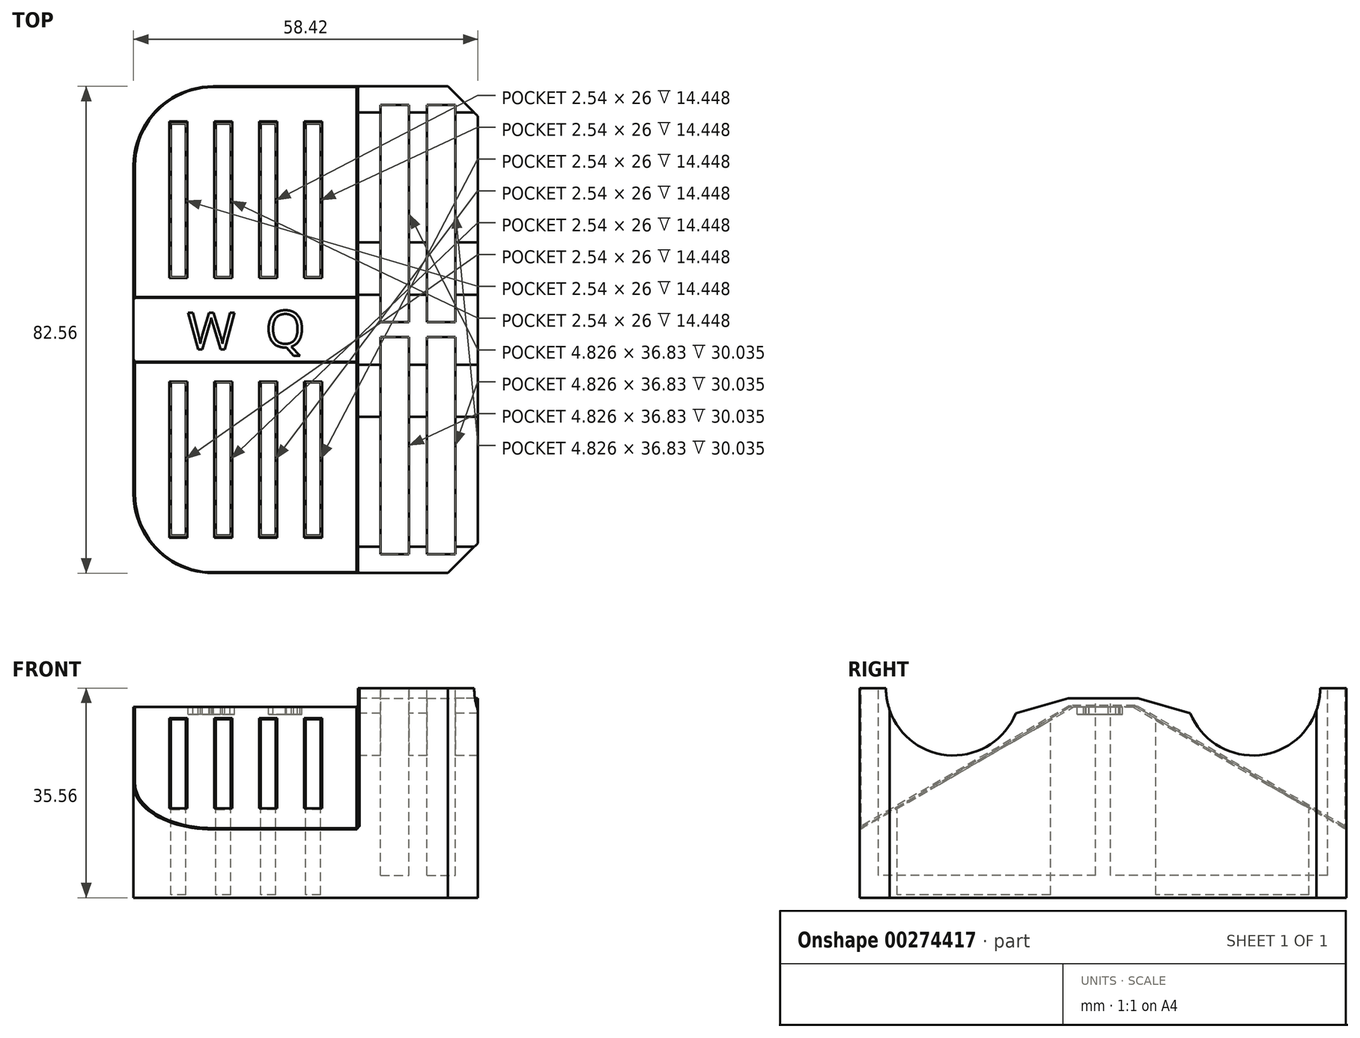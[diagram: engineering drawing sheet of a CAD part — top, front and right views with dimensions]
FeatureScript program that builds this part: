
annotation { "Feature Type Name" : "Feature", "Feature Type Description" : "" }
export const myFeature = defineFeature(function(context is Context, id is Id, definition is map)
    precondition{}
    {
        {
            var Q0;
            Q0=qCreatedBy(makeId("Top.planeOp"),FACE);
            var sketch = newSketch(context, id + "F0", { "sketchPlane" : qUnion([Q0])});
            skLineSegment(sketch, "E0.bottom", {"start": v(-29.2, 41.28) * mm, "end": v(29.21, 41.28) * mm});
            skLineSegment(sketch, "E0.top", {"start": v(-29.21, -41.27) * mm, "end": v(29.2, -41.27) * mm});
            skLineSegment(sketch, "E0.left", {"start": v(-29.2, 41.28) * mm, "end": v(-29.21, -41.27) * mm});
            skLineSegment(sketch, "E0.right", {"start": v(29.21, 41.28) * mm, "end": v(29.2, -41.27) * mm});
            skPoint(sketch, "E0.middle", {"position": v(0, 0) * mm});
            skSolve(sketch);
        }
        {
            var Q0;
            Q0=makeQuery(id+"F0.imprint","IMPRINT",FACE,{"disambiguationData":[TD([[makeQuery(id+"F0.imprint","IMPRINT",EDGE,{"derivedFrom":sQuery(id+"F0.wireOp",EDGE,"E0.bottom")}),-1.0]])]});
            extrude(context, id + "F1", {"entities" : qUnion([Q0]), "depth" : 35.56 * mm});
        }
        {
            var Q0;
            Q0=makeQuery(id+"F1.opExtrude","CAP_FACE",FACE,{"disambiguationData":[OSD([sQuery(id+"F0.wireOp",EDGE,"E0.bottom"),sQuery(id+"F0.wireOp",EDGE,"E0.top"),sQuery(id+"F0.wireOp",EDGE,"E0.left"),sQuery(id+"F0.wireOp",EDGE,"E0.right")])],"isStart":false});
            var sketch = newSketch(context, id + "F2", { "sketchPlane" : qUnion([Q0])});
            skLineSegment(sketch, "E1", {"start": v(-22.86, -8.92) * mm, "end": v(-22.86, -34.92) * mm});
            skLineSegment(sketch, "E2", {"start": v(-22.86, -34.92) * mm, "end": v(-20.32, -34.92) * mm});
            skLineSegment(sketch, "E3", {"start": v(-20.32, -34.92) * mm, "end": v(-20.32, -8.92) * mm});
            skLineSegment(sketch, "E4", {"start": v(-20.32, -8.92) * mm, "end": v(-22.86, -8.92) * mm});
            skLineSegment(sketch, "E5", {"start": v(-15.24, -8.92) * mm, "end": v(-15.24, -34.92) * mm});
            skLineSegment(sketch, "E6", {"start": v(-15.24, -34.92) * mm, "end": v(-12.7, -34.92) * mm});
            skLineSegment(sketch, "E7", {"start": v(-12.7, -34.92) * mm, "end": v(-12.7, -8.92) * mm});
            skLineSegment(sketch, "E8", {"start": v(-12.7, -8.92) * mm, "end": v(-15.24, -8.92) * mm});
            skLineSegment(sketch, "E9", {"start": v(-7.62, -8.92) * mm, "end": v(-7.62, -34.92) * mm});
            skLineSegment(sketch, "E10", {"start": v(-7.62, -34.92) * mm, "end": v(-5.08, -34.92) * mm});
            skLineSegment(sketch, "E11", {"start": v(-5.08, -34.92) * mm, "end": v(-5.08, -8.92) * mm});
            skLineSegment(sketch, "E12", {"start": v(-5.08, -8.92) * mm, "end": v(-7.62, -8.92) * mm});
            skLineSegment(sketch, "E13", {"start": v(0, -8.92) * mm, "end": v(0, -34.92) * mm});
            skLineSegment(sketch, "E14", {"start": v(0, -34.92) * mm, "end": v(2.54, -34.92) * mm});
            skLineSegment(sketch, "E15", {"start": v(2.54, -34.92) * mm, "end": v(2.54, -8.92) * mm});
            skLineSegment(sketch, "E16", {"start": v(2.54, -8.92) * mm, "end": v(0, -8.92) * mm});
            skLineSegment(sketch, "E17", {"start": v(-22.86, 34.93) * mm, "end": v(-22.86, 8.93) * mm});
            skLineSegment(sketch, "E18", {"start": v(-22.86, 8.93) * mm, "end": v(-20.32, 8.93) * mm});
            skLineSegment(sketch, "E19", {"start": v(-20.32, 8.93) * mm, "end": v(-20.32, 34.93) * mm});
            skLineSegment(sketch, "E20", {"start": v(-20.32, 34.93) * mm, "end": v(-22.86, 34.93) * mm});
            skLineSegment(sketch, "E21", {"start": v(-15.24, 34.93) * mm, "end": v(-15.24, 8.93) * mm});
            skLineSegment(sketch, "E22", {"start": v(-15.24, 8.93) * mm, "end": v(-12.7, 8.93) * mm});
            skLineSegment(sketch, "E23", {"start": v(-12.7, 8.93) * mm, "end": v(-12.7, 34.93) * mm});
            skLineSegment(sketch, "E24", {"start": v(-12.7, 34.93) * mm, "end": v(-15.24, 34.93) * mm});
            skLineSegment(sketch, "E25", {"start": v(-7.62, 34.93) * mm, "end": v(-7.62, 8.93) * mm});
            skLineSegment(sketch, "E26", {"start": v(-7.62, 8.93) * mm, "end": v(-5.08, 8.93) * mm});
            skLineSegment(sketch, "E27", {"start": v(-5.08, 8.93) * mm, "end": v(-5.08, 34.93) * mm});
            skLineSegment(sketch, "E28", {"start": v(-5.08, 34.93) * mm, "end": v(-7.62, 34.93) * mm});
            skLineSegment(sketch, "E29", {"start": v(0, 34.93) * mm, "end": v(0, 8.93) * mm});
            skLineSegment(sketch, "E30", {"start": v(0, 8.93) * mm, "end": v(2.54, 8.93) * mm});
            skLineSegment(sketch, "E31", {"start": v(2.54, 8.93) * mm, "end": v(2.54, 34.93) * mm});
            skLineSegment(sketch, "E32", {"start": v(2.54, 34.93) * mm, "end": v(0, 34.93) * mm});
            skSolve(sketch);
        }
        {
            var Q0;
            Q0=makeQuery(id+"F2.imprint","IMPRINT",FACE,{"disambiguationData":[TD([[makeQuery(id+"F2.imprint","IMPRINT",EDGE,{"derivedFrom":sQuery(id+"F2.wireOp",EDGE,"E17")}),1.0]])]});
            var Q1;
            Q1=makeQuery(id+"F2.imprint","IMPRINT",FACE,{"disambiguationData":[TD([[makeQuery(id+"F2.imprint","IMPRINT",EDGE,{"derivedFrom":sQuery(id+"F2.wireOp",EDGE,"E21")}),1.0]])]});
            var Q2;
            Q2=makeQuery(id+"F2.imprint","IMPRINT",FACE,{"disambiguationData":[TD([[makeQuery(id+"F2.imprint","IMPRINT",EDGE,{"derivedFrom":sQuery(id+"F2.wireOp",EDGE,"E25")}),1.0]])]});
            var Q3;
            Q3=makeQuery(id+"F2.imprint","IMPRINT",FACE,{"disambiguationData":[TD([[makeQuery(id+"F2.imprint","IMPRINT",EDGE,{"derivedFrom":sQuery(id+"F2.wireOp",EDGE,"E29")}),1.0]])]});
            var Q4;
            Q4=makeQuery(id+"F2.imprint","IMPRINT",FACE,{"disambiguationData":[TD([[makeQuery(id+"F2.imprint","IMPRINT",EDGE,{"derivedFrom":sQuery(id+"F2.wireOp",EDGE,"E13")}),1.0]])]});
            var Q5;
            Q5=makeQuery(id+"F2.imprint","IMPRINT",FACE,{"disambiguationData":[TD([[makeQuery(id+"F2.imprint","IMPRINT",EDGE,{"derivedFrom":sQuery(id+"F2.wireOp",EDGE,"E9")}),1.0]])]});
            var Q6;
            Q6=makeQuery(id+"F2.imprint","IMPRINT",FACE,{"disambiguationData":[TD([[makeQuery(id+"F2.imprint","IMPRINT",EDGE,{"derivedFrom":sQuery(id+"F2.wireOp",EDGE,"E5")}),1.0]])]});
            var Q7;
            Q7=makeQuery(id+"F2.imprint","IMPRINT",FACE,{"disambiguationData":[TD([[makeQuery(id+"F2.imprint","IMPRINT",EDGE,{"derivedFrom":sQuery(id+"F2.wireOp",EDGE,"E1")}),1.0]])]});
            extrude(context, id + "F3", {"entities" : qUnion([Q0, Q1, Q2, Q3, Q4, Q5, Q6, Q7]), "operationType" : NewBodyOperationType.REMOVE, "oppositeDirection" : true, "depth" : 35.05 * mm});
        }
        {
            var Q0;
            Q0=makeQuery(id+"F1.opExtrude","SWEPT_FACE",FACE,{"disambiguationData":[OSD([sQuery(id+"F0.wireOp",EDGE,"E0.left")])]});
            var sketch = newSketch(context, id + "F4", { "sketchPlane" : qUnion([Q0])});
            skLineSegment(sketch, "E33", {"start": v(0, 35.56) * mm, "end": v(-41.28, 11.73) * mm});
            skLineSegment(sketch, "E34", {"start": v(0, 35.56) * mm, "end": v(41.27, 11.73) * mm});
            skLineSegment(sketch, "E35", {"start": v(-5.53, 32.37) * mm, "end": v(5.53, 32.37) * mm});
            skSolve(sketch);
        }
        {
            var Q0;
            {var subQ0=sQuery(id+"F4.wireOp",EDGE,"E33");Q0=makeQuery(id+"F4.imprint","IMPRINT",FACE,{"disambiguationData":[TD([[makeQuery(id+"F4.imprint","IMPRINT",EDGE,{"derivedFrom":subQ0}),-1.0]])]});}
            var Q1;
            {var subQ0=sQuery(id+"F4.wireOp",EDGE,"E34");Q1=makeQuery(id+"F4.imprint","IMPRINT",FACE,{"disambiguationData":[TD([[makeQuery(id+"F4.imprint","IMPRINT",EDGE,{"derivedFrom":subQ0}),1.0]])]});}
            var Q2;
            {var subQ3=sQuery(id+"F4.wireOp",EDGE,"E35");Q2=makeQuery(id+"F4.imprint","IMPRINT",FACE,{"disambiguationData":[TD([[makeQuery(id+"F4.imprint","IMPRINT",EDGE,{"derivedFrom":subQ3}),1.0]])]});}
            extrude(context, id + "F5", {"entities" : qUnion([Q0, Q1, Q2]), "operationType" : NewBodyOperationType.REMOVE, "oppositeDirection" : true, "depth" : 38.1 * mm});
        }
        {
            var Q0;
            Q0=makeQuery(id+"F1.opExtrude","CAP_FACE",FACE,{"disambiguationData":[OSD([sQuery(id+"F0.wireOp",EDGE,"E0.bottom"),sQuery(id+"F0.wireOp",EDGE,"E0.top"),sQuery(id+"F0.wireOp",EDGE,"E0.left"),sQuery(id+"F0.wireOp",EDGE,"E0.right")])],"isStart":false});
            var sketch = newSketch(context, id + "F6", { "sketchPlane" : qUnion([Q0])});
            skLineSegment(sketch, "E36.bottom", {"start": v(12.7, -1.27) * mm, "end": v(17.53, -1.27) * mm});
            skLineSegment(sketch, "E36.top", {"start": v(12.7, -38.1) * mm, "end": v(17.53, -38.1) * mm});
            skLineSegment(sketch, "E36.left", {"start": v(12.7, -1.27) * mm, "end": v(12.7, -38.1) * mm});
            skLineSegment(sketch, "E36.right", {"start": v(17.53, -1.27) * mm, "end": v(17.53, -38.1) * mm});
            skLineSegment(sketch, "E37.bottom", {"start": v(12.7, 38.1) * mm, "end": v(17.53, 38.1) * mm});
            skLineSegment(sketch, "E37.top", {"start": v(12.7, 1.27) * mm, "end": v(17.53, 1.27) * mm});
            skLineSegment(sketch, "E37.left", {"start": v(12.7, 38.1) * mm, "end": v(12.7, 1.27) * mm});
            skLineSegment(sketch, "E37.right", {"start": v(17.53, 38.1) * mm, "end": v(17.53, 1.27) * mm});
            skLineSegment(sketch, "E38.bottom", {"start": v(20.57, 38.1) * mm, "end": v(25.4, 38.1) * mm});
            skLineSegment(sketch, "E38.top", {"start": v(20.57, 1.27) * mm, "end": v(25.4, 1.27) * mm});
            skLineSegment(sketch, "E38.left", {"start": v(20.57, 38.1) * mm, "end": v(20.57, 1.27) * mm});
            skLineSegment(sketch, "E38.right", {"start": v(25.4, 38.1) * mm, "end": v(25.4, 1.27) * mm});
            skLineSegment(sketch, "E39.bottom", {"start": v(20.57, -1.27) * mm, "end": v(25.4, -1.27) * mm});
            skLineSegment(sketch, "E39.top", {"start": v(20.57, -38.1) * mm, "end": v(25.4, -38.1) * mm});
            skLineSegment(sketch, "E39.left", {"start": v(20.57, -1.27) * mm, "end": v(20.57, -38.1) * mm});
            skLineSegment(sketch, "E39.right", {"start": v(25.4, -1.27) * mm, "end": v(25.4, -38.1) * mm});
            skSolve(sketch);
        }
        {
            var Q0;
            Q0=makeQuery(id+"F6.imprint","IMPRINT",FACE,{"disambiguationData":[TD([[makeQuery(id+"F6.imprint","IMPRINT",EDGE,{"derivedFrom":sQuery(id+"F6.wireOp",EDGE,"E37.bottom")}),-1.0]])]});
            var Q1;
            Q1=makeQuery(id+"F6.imprint","IMPRINT",FACE,{"disambiguationData":[TD([[makeQuery(id+"F6.imprint","IMPRINT",EDGE,{"derivedFrom":sQuery(id+"F6.wireOp",EDGE,"E38.bottom")}),-1.0]])]});
            var Q2;
            Q2=makeQuery(id+"F6.imprint","IMPRINT",FACE,{"disambiguationData":[TD([[makeQuery(id+"F6.imprint","IMPRINT",EDGE,{"derivedFrom":sQuery(id+"F6.wireOp",EDGE,"E36.bottom")}),-1.0]])]});
            var Q3;
            Q3=makeQuery(id+"F6.imprint","IMPRINT",FACE,{"disambiguationData":[TD([[makeQuery(id+"F6.imprint","IMPRINT",EDGE,{"derivedFrom":sQuery(id+"F6.wireOp",EDGE,"E39.bottom")}),-1.0]])]});
            extrude(context, id + "F7", {"entities" : qUnion([Q0, Q1, Q2, Q3]), "operationType" : NewBodyOperationType.REMOVE, "oppositeDirection" : true, "depth" : 31.75 * mm});
        }
        {
            var Q0;
            Q0=makeQuery(id+"F5.boolean.opBoolean","COPY",FACE,{"derivedFrom":makeQuery(id+"F5.opExtrude","SWEPT_FACE",FACE,{"disambiguationData":[OSD([sQuery(id+"F4.wireOp",EDGE,"E35")])]})});
            var sketch = newSketch(context, id + "F8", { "sketchPlane" : qUnion([Q0])});
            skText(sketch, "E40", { "text": "W", "fontName": "OpenSans-Regular.ttf"});
            skText(sketch, "E41", { "text": "Q\n", "fontName": "OpenSans-Regular.ttf"});
            const initialGuessF8  = {"E40": [-0.02004, -0.00333, 1, 0, 0.0063], "E41": [-0.00682, -0.00293, 1, 0, 0.0062]};
            skSetInitialGuess(sketch, initialGuessF8);
            skSolve(sketch);
        }
        {
            var Q0;
            Q0=qSketchRegion(id+"F8",true);
            extrude(context, id + "F9", {"entities" : qUnion([Q0]), "operationType" : NewBodyOperationType.REMOVE, "oppositeDirection" : true, "depth" : 1.27 * mm});
        }
        {
            var Q0;
            Q0=makeQuery(id+"F5.boolean.opBoolean","COPY",FACE,{"derivedFrom":makeQuery(id+"F5.opExtrude","CAP_FACE",FACE,{"disambiguationData":[OSD([sQuery(id+"F0.wireOp",EDGE,"E0.bottom"),sQuery(id+"F0.wireOp",EDGE,"E0.top"),sQuery(id+"F0.wireOp",EDGE,"E0.left"),sQuery(id+"F4.wireOp",EDGE,"E33"),sQuery(id+"F4.wireOp",EDGE,"E34"),sQuery(id+"F4.wireOp",EDGE,"E35")])],"isStart":false})});
            var sketch = newSketch(context, id + "F10", { "sketchPlane" : qUnion([Q0])});
            skLineSegment(sketch, "E42", {"start": v(-41.28, 23.64) * mm, "end": v(0, 35.56) * mm});
            skLineSegment(sketch, "E43", {"start": v(0, 35.56) * mm, "end": v(41.27, 23.64) * mm});
            skLineSegment(sketch, "E44", {"start": v(-1.27, 35.2) * mm, "end": v(1.27, 35.2) * mm});
            skArc(sketch, "E45", {"start": v(-35.56, 40.8) * mm, "mid": v(-28.1, 24.45) * mm, "end": v(-13.97, 35.56) * mm});
            skArc(sketch, "E46", {"start": v(13.97, 35.56) * mm, "mid": v(25.4, 24.13) * mm, "end": v(36.83, 35.56) * mm});
            skLineSegment(sketch, "E47", {"start": v(-14.1, 33.85) * mm, "end": v(14.1, 33.85) * mm});
            skSolve(sketch);
        }
        {
            var Q0;
            {var subQ0=sQuery(id+"F10.wireOp",EDGE,"E45");var subQ1=sQuery(id+"F10.wireOp",EDGE,"E42");var subQ2=makeQuery(id+"F10.imprint","INTERSECT",VERTEX,{"disambiguationData":[OD(0.0)],"derivedFrom":[subQ1,subQ0]});Q0=makeQuery(id+"F10.imprint","IMPRINT",FACE,{"disambiguationData":[TD([[makeQuery(id+"F10.imprint","IMPRINT",EDGE,{"disambiguationData":[TD([[subQ2,-1.0]])],"derivedFrom":subQ1}),-1.0]])]});}
            var Q1;
            {var subQ0=sQuery(id+"F10.wireOp",EDGE,"E46");var subQ1=sQuery(id+"F10.wireOp",EDGE,"E43");var subQ2=makeQuery(id+"F10.imprint","INTERSECT",VERTEX,{"disambiguationData":[OD(0.0)],"derivedFrom":[subQ1,subQ0]});Q1=makeQuery(id+"F10.imprint","IMPRINT",FACE,{"disambiguationData":[TD([[makeQuery(id+"F10.imprint","IMPRINT",EDGE,{"disambiguationData":[TD([[subQ2,-1.0]])],"derivedFrom":subQ1}),1.0]])]});}
            var Q2;
            {var subQ0=sQuery(id+"F10.wireOp",EDGE,"E46");var subQ1=sQuery(id+"F10.wireOp",EDGE,"E43");var subQ2=makeQuery(id+"F10.imprint","INTERSECT",VERTEX,{"disambiguationData":[OD(0.0)],"derivedFrom":[subQ1,subQ0]});Q2=makeQuery(id+"F10.imprint","IMPRINT",FACE,{"disambiguationData":[TD([[makeQuery(id+"F10.imprint","IMPRINT",EDGE,{"disambiguationData":[TD([[subQ2,-1.0]])],"derivedFrom":subQ1}),-1.0]])]});}
            var Q3;
            {var subQ0=sQuery(id+"F10.wireOp",EDGE,"E45");var subQ1=sQuery(id+"F10.wireOp",EDGE,"E42");var subQ2=makeQuery(id+"F10.imprint","INTERSECT",VERTEX,{"disambiguationData":[OD(0.0)],"derivedFrom":[subQ1,subQ0]});Q3=makeQuery(id+"F10.imprint","IMPRINT",FACE,{"disambiguationData":[TD([[makeQuery(id+"F10.imprint","IMPRINT",EDGE,{"disambiguationData":[TD([[subQ2,-1.0]])],"derivedFrom":subQ1}),1.0]])]});}
            var Q4;
            {var subQ0=sQuery(id+"F10.wireOp",EDGE,"E44");Q4=makeQuery(id+"F10.imprint","IMPRINT",FACE,{"disambiguationData":[TD([[makeQuery(id+"F10.imprint","IMPRINT",EDGE,{"derivedFrom":subQ0}),-1.0]])]});}
            var Q5;
            {var subQ3=sQuery(id+"F10.wireOp",EDGE,"E42");var subQ8=makeQuery(id+"F10.imprint","INTERSECT",VERTEX,{"derivedFrom":[subQ3,sQuery(id+"F10.wireOp",EDGE,"E44")]});Q5=makeQuery(id+"F10.imprint","IMPRINT",FACE,{"disambiguationData":[TD([[makeQuery(id+"F10.imprint","IMPRINT",EDGE,{"disambiguationData":[TD([[subQ8,1.0]])],"derivedFrom":subQ3}),1.0]])]});}
            var Q6;
            {var subQ3=sQuery(id+"F10.wireOp",EDGE,"E43");var subQ5=makeQuery(id+"F10.imprint","INTERSECT",VERTEX,{"derivedFrom":[subQ3,sQuery(id+"F10.wireOp",EDGE,"E44")]});Q6=makeQuery(id+"F10.imprint","IMPRINT",FACE,{"disambiguationData":[TD([[makeQuery(id+"F10.imprint","IMPRINT",EDGE,{"disambiguationData":[TD([[subQ5,-1.0]])],"derivedFrom":subQ3}),1.0]])]});}
            var Q7;
            {var subQ3=sQuery(id+"F10.wireOp",EDGE,"E44");Q7=makeQuery(id+"F10.imprint","IMPRINT",FACE,{"disambiguationData":[TD([[makeQuery(id+"F10.imprint","IMPRINT",EDGE,{"derivedFrom":subQ3}),1.0]])]});}
            var Q8;
            {var subQ0=sQuery(id+"F10.wireOp",EDGE,"E45");var subQ1=sQuery(id+"F10.wireOp",EDGE,"E42");var subQ2=makeQuery(id+"F10.imprint","INTERSECT",VERTEX,{"disambiguationData":[OD(1.0)],"derivedFrom":[subQ1,subQ0]});Q8=makeQuery(id+"F10.imprint","IMPRINT",FACE,{"disambiguationData":[TD([[makeQuery(id+"F10.imprint","IMPRINT",EDGE,{"disambiguationData":[TD([[subQ2,-1.0]])],"derivedFrom":subQ1}),1.0]])]});}
            var Q9;
            {var subQ0=sQuery(id+"F10.wireOp",EDGE,"E47");var subQ1=sQuery(id+"F10.wireOp",EDGE,"E43");var subQ2=makeQuery(id+"F10.imprint","INTERSECT",VERTEX,{"derivedFrom":[subQ1,subQ0]});Q9=makeQuery(id+"F10.imprint","IMPRINT",FACE,{"disambiguationData":[TD([[makeQuery(id+"F10.imprint","IMPRINT",EDGE,{"disambiguationData":[TD([[subQ2,-1.0]])],"derivedFrom":subQ1}),1.0]])]});}
            extrude(context, id + "F11", {"entities" : qUnion([Q0, Q1, Q2, Q3, Q4, Q5, Q6, Q7, Q8, Q9]), "operationType" : NewBodyOperationType.REMOVE, "oppositeDirection" : true, "depth" : 25.4 * mm});
        }
        {
            var Q0;
            Q0=makeQuery(id+"F1.opExtrude","SWEPT_EDGE",EDGE,{"disambiguationData":[OSD([sQuery(id+"F0.wireOp",EDGE,"E0.bottom"),sQuery(id+"F0.wireOp",EDGE,"E0.left")])]});
            var Q1;
            Q1=makeQuery(id+"F1.opExtrude","SWEPT_EDGE",EDGE,{"disambiguationData":[OSD([sQuery(id+"F0.wireOp",EDGE,"E0.top"),sQuery(id+"F0.wireOp",EDGE,"E0.left")])]});
            fillet(context, id + "F12", {"entities" : qUnion([Q0, Q1]), "radius" : 13.5 * mm, "tangentPropagation" : true, "allowEdgeOverflow" : false});
        }
        {
            var Q0;
            Q0=makeQuery(id+"F5.boolean.opBoolean","COPY",FACE,{"derivedFrom":makeQuery(id+"F5.opExtrude","SWEPT_FACE",FACE,{"disambiguationData":[OSD([sQuery(id+"F4.wireOp",EDGE,"E33")])]})});
            var Q1;
            Q1=makeQuery(id+"F5.boolean.opBoolean","COPY",FACE,{"derivedFrom":makeQuery(id+"F5.opExtrude","SWEPT_FACE",FACE,{"disambiguationData":[OSD([sQuery(id+"F4.wireOp",EDGE,"E34")])]})});
            chamfer(context, id + "F13", {"entities" : qUnion([Q0, Q1]), "width" : 0.25 * mm, "tangentPropagation" : true});
        }
        {
            var Q0;
            Q0=makeQuery(id+"F1.opExtrude","SWEPT_EDGE",EDGE,{"disambiguationData":[OSD([sQuery(id+"F0.wireOp",EDGE,"E0.top"),sQuery(id+"F0.wireOp",EDGE,"E0.right")])]});
            var Q1;
            Q1=makeQuery(id+"F1.opExtrude","SWEPT_EDGE",EDGE,{"disambiguationData":[OSD([sQuery(id+"F0.wireOp",EDGE,"E0.bottom"),sQuery(id+"F0.wireOp",EDGE,"E0.right")])]});
            var Q2;
            Q2=makeQuery(id+"F5.boolean.opBoolean","COPY",EDGE,{"derivedFrom":makeQuery(id+"F5.opExtrude","CAP_EDGE",EDGE,{"disambiguationData":[OSD([sQuery(id+"F0.wireOp",EDGE,"E0.top"),sQuery(id+"F0.wireOp",EDGE,"E0.left")])],"isStart":false})});
            var Q3;
            Q3=makeQuery(id+"F5.boolean.opBoolean","COPY",EDGE,{"derivedFrom":makeQuery(id+"F5.opExtrude","CAP_EDGE",EDGE,{"disambiguationData":[OSD([sQuery(id+"F0.wireOp",EDGE,"E0.bottom"),sQuery(id+"F0.wireOp",EDGE,"E0.left")])],"isStart":false})});
            chamfer(context, id + "F14", {"entities" : qUnion([Q0, Q1, Q2, Q3]), "width" : 5.08 * mm, "tangentPropagation" : true});
        }
    });
